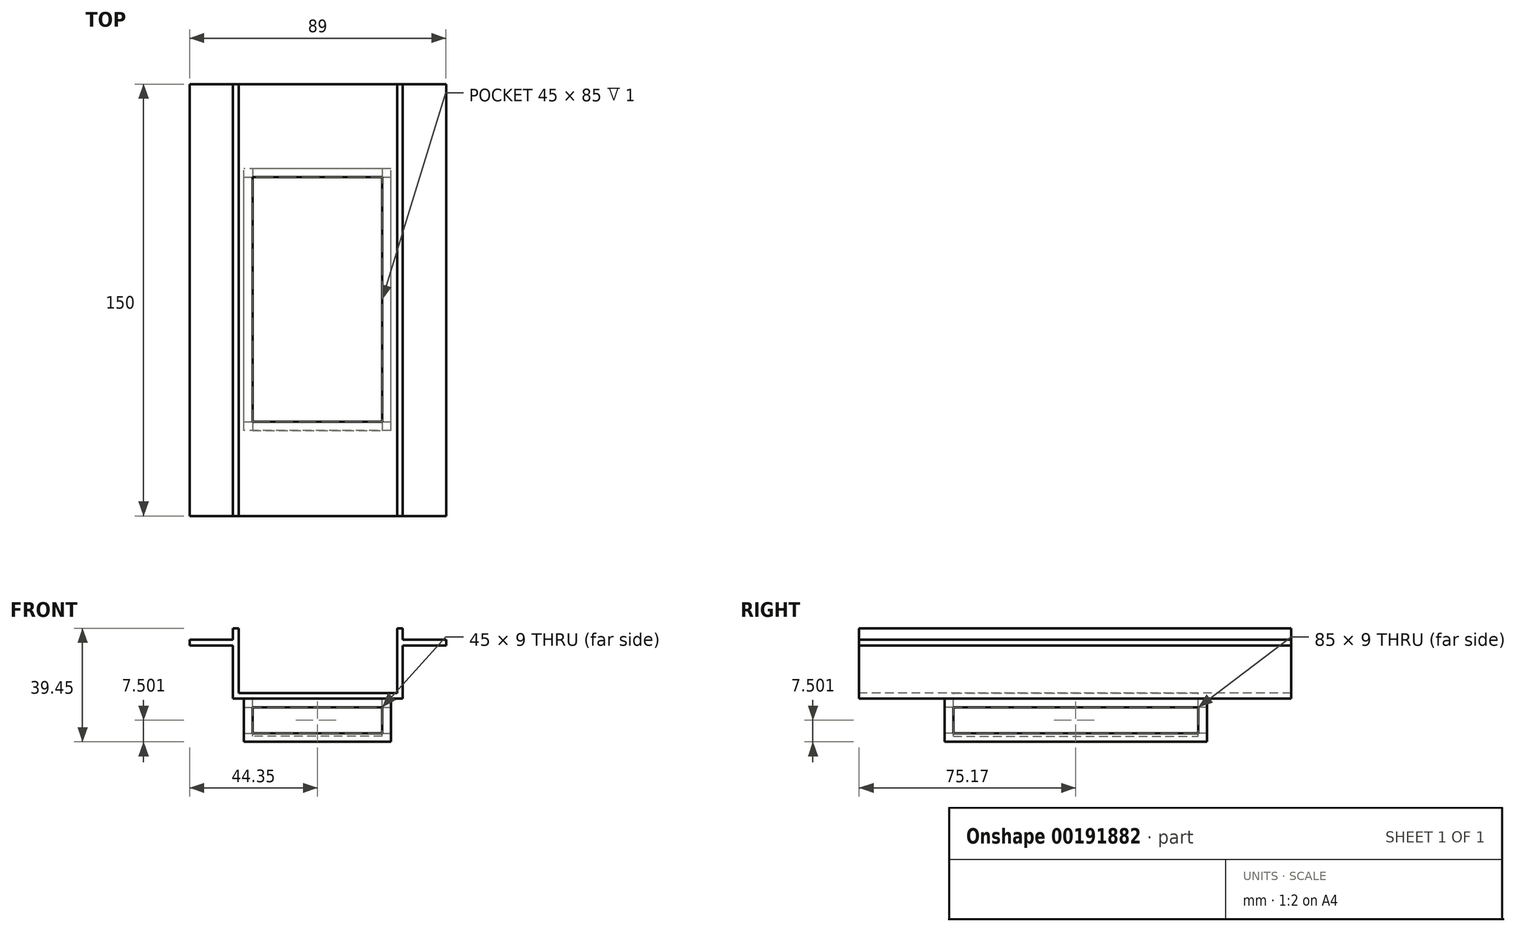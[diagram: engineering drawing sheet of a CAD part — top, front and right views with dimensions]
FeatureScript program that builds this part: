
annotation { "Feature Type Name" : "Feature", "Feature Type Description" : "" }
export const myFeature = defineFeature(function(context is Context, id is Id, definition is map)
    precondition{}
    {
        {
            var Q0;
            Q0=qCreatedBy(makeId("Front.planeOp"),FACE);
            var sketch = newSketch(context, id + "F0", { "sketchPlane" : qUnion([Q0])});
            skLineSegment(sketch, "E0.bottom", {"start": v(29.65, -10.12) * mm, "end": v(-29.35, -10.12) * mm});
            skLineSegment(sketch, "E0.left", {"start": v(29.65, -10.12) * mm, "end": v(29.65, 10.33) * mm});
            skLineSegment(sketch, "E0.right", {"start": v(-29.35, -10.12) * mm, "end": v(-29.35, 10.33) * mm});
            skPoint(sketch, "E0.middle", {"position": v(0.15, 0.1) * mm});
            skLineSegment(sketch, "E1.left", {"start": v(27.65, -9) * mm, "end": v(27.65, 9.22) * mm});
            skLineSegment(sketch, "E1.right", {"start": v(-27.35, -9) * mm, "end": v(-27.35, 9.22) * mm});
            skLineSegment(sketch, "E2", {"start": v(-27.35, 9.22) * mm, "end": v(-27.35, 10.33) * mm});
            skLineSegment(sketch, "E3", {"start": v(27.65, 9.22) * mm, "end": v(27.65, 10.33) * mm});
            skLineSegment(sketch, "E4.left", {"start": v(-24.65, 1.23) * mm, "end": v(-24.65, 1.23) * mm});
            skLineSegment(sketch, "E4.right", {"start": v(-22.65, 1.23) * mm, "end": v(-22.65, 1.23) * mm});
            skLineSegment(sketch, "E5", {"start": v(-29.35, 10.33) * mm, "end": v(-29.35, 14.33) * mm});
            skLineSegment(sketch, "E6", {"start": v(-29.35, 14.33) * mm, "end": v(-27.35, 14.33) * mm});
            skLineSegment(sketch, "E7", {"start": v(-27.35, 14.33) * mm, "end": v(-27.35, -9) * mm});
            skLineSegment(sketch, "E8", {"start": v(29.65, 10.33) * mm, "end": v(29.65, 14.33) * mm});
            skLineSegment(sketch, "E9", {"start": v(29.65, 14.33) * mm, "end": v(27.65, 14.33) * mm});
            skLineSegment(sketch, "E10", {"start": v(27.65, 14.33) * mm, "end": v(27.65, -9) * mm});
            skLineSegment(sketch, "E11", {"start": v(-27.35, -8.12) * mm, "end": v(27.65, -8.12) * mm});
            skLineSegment(sketch, "E12.bottom", {"start": v(-29.35, 10.33) * mm, "end": v(-44.35, 10.33) * mm});
            skLineSegment(sketch, "E12.top", {"start": v(-29.35, 8.33) * mm, "end": v(-44.35, 8.33) * mm});
            skLineSegment(sketch, "E12.left", {"start": v(-29.35, 10.33) * mm, "end": v(-29.35, 8.33) * mm});
            skLineSegment(sketch, "E12.right", {"start": v(-44.35, 10.33) * mm, "end": v(-44.35, 8.33) * mm});
            skLineSegment(sketch, "E13.bottom", {"start": v(29.65, 10.33) * mm, "end": v(44.65, 10.33) * mm});
            skLineSegment(sketch, "E13.top", {"start": v(29.65, 8.33) * mm, "end": v(44.65, 8.33) * mm});
            skLineSegment(sketch, "E13.left", {"start": v(29.65, 10.33) * mm, "end": v(29.65, 8.33) * mm});
            skLineSegment(sketch, "E13.right", {"start": v(44.65, 10.33) * mm, "end": v(44.65, 8.33) * mm});
            skLineSegment(sketch, "E14.right", {"start": v(-30.69, 10.34) * mm, "end": v(-30.69, 8.34) * mm});
            skLineSegment(sketch, "E15.right", {"start": v(41.5, 10.34) * mm, "end": v(41.5, 8.34) * mm});
            skLineSegment(sketch, "E16", {"start": v(0, 35.06) * mm, "end": v(0, -19.3) * mm, "construction": true});
            skArc(sketch, "E17", {"start": v(29.65, 14.33) * mm, "mid": v(30.7, 11.61) * mm, "end": v(33.32, 10.33) * mm});
            skArc(sketch, "E18", {"start": v(-32.7, 10.33) * mm, "mid": v(-30.3, 11.72) * mm, "end": v(-29.35, 14.33) * mm});
            skSolve(sketch);
        }
        {
            var Q0;
            Q0=makeQuery(id+"F0.imprint","IMPRINT",FACE,{"disambiguationData":[TD([[makeQuery(id+"F0.imprint","IMPRINT",EDGE,{"derivedFrom":sQuery(id+"F0.wireOp",EDGE,"E12.top")}),-1.0]])]});
            var Q1;
            Q1=makeQuery(id+"F0.imprint","IMPRINT",FACE,{"disambiguationData":[TD([[makeQuery(id+"F0.imprint","IMPRINT",EDGE,{"derivedFrom":sQuery(id+"F0.wireOp",EDGE,"E0.bottom")}),-1.0]])]});
            var Q2;
            Q2=makeQuery(id+"F0.imprint","IMPRINT",FACE,{"disambiguationData":[TD([[makeQuery(id+"F0.imprint","IMPRINT",EDGE,{"derivedFrom":sQuery(id+"F0.wireOp",EDGE,"E13.top")}),1.0]])]});
            extrude(context, id + "F1", {"entities" : qUnion([Q0, Q1, Q2]), "oppositeDirection" : true, "depth" : 150 * mm});
        }
        {
            var Q0;
            Q0=makeQuery(id+"F1.opExtrude","SWEPT_FACE",FACE,{"disambiguationData":[OSD([sQuery(id+"F0.wireOp",EDGE,"E11")])]});
            var sketch = newSketch(context, id + "F2", { "sketchPlane" : qUnion([Q0])});
            skLineSegment(sketch, "E19.bottom", {"start": v(22.5, 32.67) * mm, "end": v(-22.5, 32.67) * mm});
            skLineSegment(sketch, "E19.top", {"start": v(22.5, 117.67) * mm, "end": v(-22.5, 117.67) * mm});
            skLineSegment(sketch, "E19.left", {"start": v(22.5, 32.67) * mm, "end": v(22.5, 117.67) * mm});
            skLineSegment(sketch, "E19.right", {"start": v(-22.5, 32.67) * mm, "end": v(-22.5, 117.67) * mm});
            skPoint(sketch, "E19.middle", {"position": v(0, 75.17) * mm});
            skLineSegment(sketch, "E20.0", {"start": v(25.5, 120.67) * mm, "end": v(-25.5, 120.67) * mm});
            skLineSegment(sketch, "E20.1", {"start": v(25.5, 29.67) * mm, "end": v(25.5, 120.67) * mm});
            skLineSegment(sketch, "E20.2", {"start": v(25.5, 29.67) * mm, "end": v(-25.5, 29.67) * mm});
            skLineSegment(sketch, "E20.3", {"start": v(-25.5, 29.67) * mm, "end": v(-25.5, 120.67) * mm});
            skSolve(sketch);
        }
        {
            var Q0;
            Q0=makeQuery(id+"F2.imprint","IMPRINT",FACE,{"disambiguationData":[TD([[makeQuery(id+"F2.imprint","IMPRINT",EDGE,{"derivedFrom":sQuery(id+"F2.wireOp",EDGE,"E19.bottom")}),-1.0]])]});
            var Q1;
            Q1=makeQuery(id+"F2.imprint","IMPRINT",FACE,{"disambiguationData":[TD([[makeQuery(id+"F2.imprint","IMPRINT",EDGE,{"derivedFrom":sQuery(id+"F2.wireOp",EDGE,"E19.bottom")}),1.0]])]});
            extrude(context, id + "F3", {"entities" : qUnion([Q0, Q1]), "operationType" : NewBodyOperationType.ADD, "oppositeDirection" : true, "depth" : 17 * mm});
        }
        {
            var Q0;
            Q0=makeQuery(id+"F2.imprint","IMPRINT",FACE,{"disambiguationData":[TD([[makeQuery(id+"F2.imprint","IMPRINT",EDGE,{"derivedFrom":sQuery(id+"F2.wireOp",EDGE,"E19.bottom")}),-1.0]])]});
            extrude(context, id + "F4", {"entities" : qUnion([Q0]), "operationType" : NewBodyOperationType.REMOVE, "oppositeDirection" : true, "depth" : 15 * mm});
        }
        {
            var Q0;
            Q0=makeQuery(id+"F3.opExtrude","SWEPT_FACE",FACE,{"disambiguationData":[OSD([sQuery(id+"F2.wireOp",EDGE,"E20.1")])]});
            var sketch = newSketch(context, id + "F5", { "sketchPlane" : qUnion([Q0])});
            skLineSegment(sketch, "E21.0", {"start": v(117.67, -13.12) * mm, "end": v(32.67, -13.12) * mm});
            skLineSegment(sketch, "E21.1", {"start": v(117.67, -22.12) * mm, "end": v(117.67, -13.12) * mm});
            skLineSegment(sketch, "E21.2", {"start": v(32.67, -22.12) * mm, "end": v(117.67, -22.12) * mm});
            skLineSegment(sketch, "E21.3", {"start": v(32.67, -13.12) * mm, "end": v(32.67, -22.12) * mm});
            skSolve(sketch);
        }
        {
            var Q0;
            Q0=makeQuery(id+"F5.imprint","IMPRINT",FACE,{"disambiguationData":[TD([[makeQuery(id+"F5.imprint","IMPRINT",EDGE,{"derivedFrom":sQuery(id+"F5.wireOp",EDGE,"E21.0")}),1.0]])]});
            extrude(context, id + "F6", {"entities" : qUnion([Q0]), "operationType" : NewBodyOperationType.REMOVE, "oppositeDirection" : true, "depth" : 75 * mm});
        }
        {
            var Q0;
            Q0=makeQuery(id+"F3.opExtrude","SWEPT_FACE",FACE,{"disambiguationData":[OSD([sQuery(id+"F2.wireOp",EDGE,"E20.2")])]});
            var sketch = newSketch(context, id + "F7", { "sketchPlane" : qUnion([Q0])});
            skLineSegment(sketch, "E22.0", {"start": v(22.5, -22.12) * mm, "end": v(22.5, -13.12) * mm});
            skLineSegment(sketch, "E22.1", {"start": v(-22.5, -22.12) * mm, "end": v(22.5, -22.12) * mm});
            skLineSegment(sketch, "E22.2", {"start": v(-22.5, -13.12) * mm, "end": v(-22.5, -22.12) * mm});
            skLineSegment(sketch, "E22.3", {"start": v(22.5, -13.12) * mm, "end": v(-22.5, -13.12) * mm});
            skSolve(sketch);
        }
        {
            var Q0;
            Q0=makeQuery(id+"F7.imprint","IMPRINT",FACE,{"disambiguationData":[TD([[makeQuery(id+"F7.imprint","IMPRINT",EDGE,{"derivedFrom":sQuery(id+"F7.wireOp",EDGE,"E22.0")}),1.0]])]});
            extrude(context, id + "F8", {"entities" : qUnion([Q0]), "operationType" : NewBodyOperationType.REMOVE, "oppositeDirection" : true, "depth" : 95 * mm});
        }
    });
